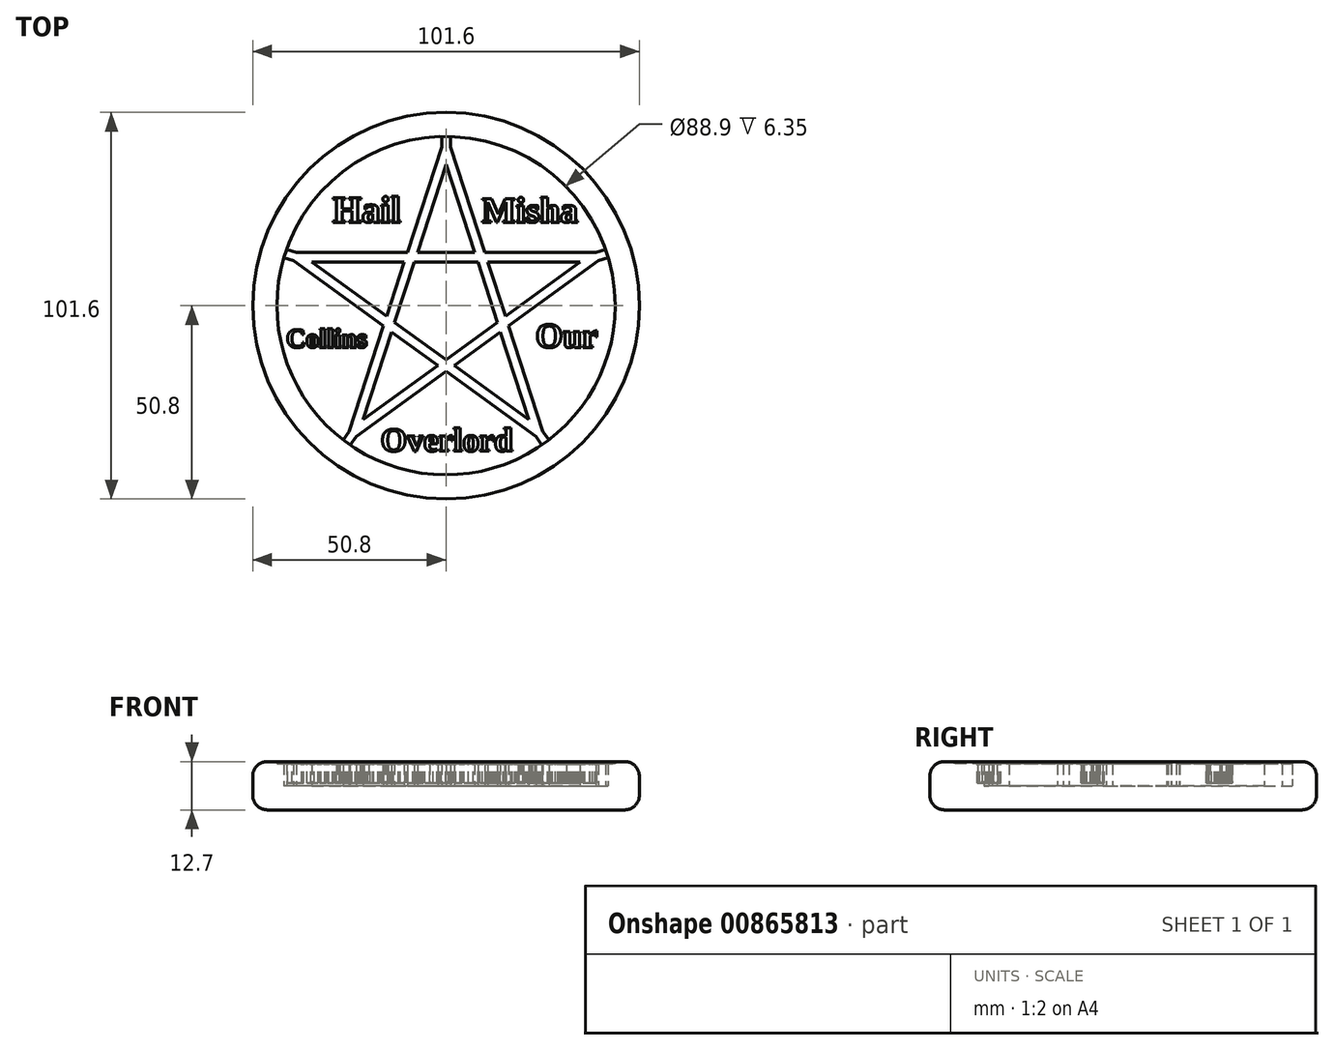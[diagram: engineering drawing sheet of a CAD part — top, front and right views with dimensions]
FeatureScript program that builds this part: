
annotation { "Feature Type Name" : "Feature", "Feature Type Description" : "" }
export const myFeature = defineFeature(function(context is Context, id is Id, definition is map)
    precondition{}
    {
        {
            var Q0;
            Q0=qCreatedBy(makeId("Top.planeOp"),FACE);
            var sketch = newSketch(context, id + "F0", { "sketchPlane" : qUnion([Q0])});
            skCircle(sketch, "E0", {"center": v(0, 0) * mm, "radius": 50.8 * mm});
            skSolve(sketch);
        }
        {
            var Q0;
            Q0=qSketchRegion(id+"F0",true);
            extrude(context, id + "F1", {"entities" : qUnion([Q0]), "depth" : 12.7 * mm, "offsetDistance" : 25.4 * mm});
        }
        {
            var Q0;
            Q0=makeQuery(id+"F1.opExtrude","CAP_FACE",FACE,{"disambiguationData":[OSD([sQuery(id+"F0.wireOp",EDGE,"E0")])],"isStart":false});
            shell(context, id + "F2", {"entities" : qUnion([Q0]), "thickness" : 6.35 * mm});
        }
        {
            var Q0;
            {var subQ0=sQuery(id+"F0.wireOp",EDGE,"E0");Q0=makeQuery(id+"F2.opShell","OFFSET_FACE",FACE,{"disambiguationData":[OSD([subQ0]),TDD([makeQuery(id+"F1.opExtrude","CAP_FACE",FACE,{"disambiguationData":[OSD([subQ0])],"isStart":true})])]});}
            var sketch = newSketch(context, id + "F3", { "sketchPlane" : qUnion([Q0])});
            skCircle(sketch, "E1.cCircle", {"center": v(0, 0) * mm, "radius": 13.97 * mm, "construction": true});
            skLineSegment(sketch, "E2", {"start": v(-10.15, 13.97) * mm, "end": v(-1.12, 41.75) * mm});
            skLineSegment(sketch, "E3", {"start": v(10.15, 13.97) * mm, "end": v(1.12, 41.75) * mm});
            skLineSegment(sketch, "E4", {"start": v(-16.42, -5.34) * mm, "end": v(-40.05, 11.83) * mm});
            skLineSegment(sketch, "E5", {"start": v(-10.15, 13.97) * mm, "end": v(-39.36, 13.97) * mm});
            skLineSegment(sketch, "E6", {"start": v(10.15, 13.97) * mm, "end": v(39.36, 13.97) * mm});
            skLineSegment(sketch, "E7", {"start": v(16.42, -5.34) * mm, "end": v(40.05, 11.83) * mm});
            skLineSegment(sketch, "E8", {"start": v(0, -17.27) * mm, "end": v(-23.63, -34.44) * mm});
            skLineSegment(sketch, "E9", {"start": v(-16.42, -5.34) * mm, "end": v(-25.45, -33.12) * mm});
            skLineSegment(sketch, "E10", {"start": v(16.42, -5.34) * mm, "end": v(25.45, -33.12) * mm});
            skLineSegment(sketch, "E11", {"start": v(0, -17.27) * mm, "end": v(23.63, -34.44) * mm});
            skLineSegment(sketch, "E12", {"start": v(39.36, 13.97) * mm, "end": v(41.93, 14.76) * mm});
            skLineSegment(sketch, "E13", {"start": v(40.05, 11.83) * mm, "end": v(42.62, 12.62) * mm});
            skLineSegment(sketch, "E14", {"start": v(1.12, 41.75) * mm, "end": v(1.12, 44.44) * mm});
            skLineSegment(sketch, "E15", {"start": v(-1.12, 41.75) * mm, "end": v(-1.12, 44.44) * mm});
            skLineSegment(sketch, "E16", {"start": v(-39.36, 13.97) * mm, "end": v(-41.91, 14.8) * mm});
            skLineSegment(sketch, "E17", {"start": v(-40.05, 11.83) * mm, "end": v(-42.6, 12.66) * mm});
            skLineSegment(sketch, "E18", {"start": v(-23.63, -34.44) * mm, "end": v(-25.2, -36.6) * mm});
            skLineSegment(sketch, "E19", {"start": v(-25.45, -33.12) * mm, "end": v(-27.03, -35.29) * mm});
            skLineSegment(sketch, "E20", {"start": v(-7.5, 13.97) * mm, "end": v(7.5, 13.97) * mm});
            skLineSegment(sketch, "E21", {"start": v(7.5, 13.97) * mm, "end": v(0, 37.06) * mm});
            skLineSegment(sketch, "E22", {"start": v(0, 37.06) * mm, "end": v(-7.5, 13.97) * mm});
            skLineSegment(sketch, "E23", {"start": v(-10.97, 11.45) * mm, "end": v(-35.25, 11.45) * mm});
            skLineSegment(sketch, "E24", {"start": v(-35.25, 11.45) * mm, "end": v(-15.6, -2.82) * mm});
            skPoint(sketch, "E25", {"position": v(-25.43, 4.32) * mm});
            skPoint(sketch, "E26", {"position": v(-28.24, 3.25) * mm});
            skPoint(sketch, "E27", {"position": v(-24.75, 13.97) * mm});
            skLineSegment(sketch, "E28", {"start": v(-14.28, -6.9) * mm, "end": v(-2.14, -15.71) * mm});
            skLineSegment(sketch, "E29", {"start": v(-2.14, -15.71) * mm, "end": v(-21.79, -29.99) * mm});
            skLineSegment(sketch, "E30", {"start": v(-21.79, -29.99) * mm, "end": v(-14.28, -6.9) * mm});
            skPoint(sketch, "E31", {"position": v(-11.96, -22.85) * mm});
            skPoint(sketch, "E32", {"position": v(-11.82, -25.85) * mm});
            skPoint(sketch, "E33", {"position": v(-18.03, -18.44) * mm});
            skPoint(sketch, "E34", {"position": v(-20.94, -19.23) * mm});
            skPoint(sketch, "E35.positionSnap0", {"position": v(-8.21, -11.3) * mm});
            skLineSegment(sketch, "E36", {"start": v(25.45, -33.12) * mm, "end": v(27.03, -35.29) * mm});
            skLineSegment(sketch, "E37", {"start": v(23.63, -34.44) * mm, "end": v(25.2, -36.6) * mm});
            skLineSegment(sketch, "E38", {"start": v(2.14, -15.71) * mm, "end": v(14.28, -6.9) * mm});
            skLineSegment(sketch, "E39", {"start": v(14.28, -6.9) * mm, "end": v(21.79, -29.99) * mm});
            skLineSegment(sketch, "E40", {"start": v(21.79, -29.99) * mm, "end": v(2.14, -15.71) * mm});
            skPoint(sketch, "E41", {"position": v(11.82, -25.85) * mm});
            skPoint(sketch, "E42.positionSnap0", {"position": v(20.94, -19.23) * mm});
            skLineSegment(sketch, "E43", {"start": v(10.97, 11.45) * mm, "end": v(15.6, -2.82) * mm});
            skLineSegment(sketch, "E44", {"start": v(15.6, -2.82) * mm, "end": v(35.25, 11.45) * mm});
            skLineSegment(sketch, "E45", {"start": v(35.25, 11.45) * mm, "end": v(10.97, 11.45) * mm});
            skPoint(sketch, "E46", {"position": v(23.1, 11.45) * mm});
            skPoint(sketch, "E47", {"position": v(24.75, 13.97) * mm});
            skPoint(sketch, "E48", {"position": v(13.29, 4.32) * mm});
            skCircle(sketch, "E49.cCircle", {"center": v(0, 0) * mm, "radius": 14.23 * mm, "construction": true});
            skLineSegment(sketch, "E49.0", {"start": v(13.53, -4.4) * mm, "end": v(0, -14.23) * mm});
            skLineSegment(sketch, "E49.1", {"start": v(0, -14.23) * mm, "end": v(-13.53, -4.4) * mm});
            skLineSegment(sketch, "E49.2", {"start": v(-13.53, -4.4) * mm, "end": v(-8.36, 11.51) * mm});
            skLineSegment(sketch, "E49.3", {"start": v(-8.36, 11.51) * mm, "end": v(8.36, 11.51) * mm});
            skLineSegment(sketch, "E49.4", {"start": v(8.36, 11.51) * mm, "end": v(13.53, -4.4) * mm});
            skLineSegment(sketch, "E50", {"start": v(-10.97, 11.45) * mm, "end": v(-15.6, -2.82) * mm});
            skPoint(sketch, "E51", {"position": v(-13.29, 4.32) * mm});
            skPoint(sketch, "E52", {"position": v(28.24, 3.25) * mm});
            skPoint(sketch, "E53.positionSnap0", {"position": v(25.43, 4.32) * mm});
            skPoint(sketch, "E54", {"position": v(-23.1, 11.45) * mm});
            skPoint(sketch, "E55", {"position": v(0, 13.97) * mm});
            skPoint(sketch, "E56", {"position": v(8.21, -11.3) * mm});
            skSolve(sketch);
        }
        {
            var Q0;
            Q0=makeQuery(id+"F1.opExtrude","CAP_EDGE",EDGE,{"disambiguationData":[OSD([sQuery(id+"F0.wireOp",EDGE,"E0")])],"isStart":false});
            fillet(context, id + "F4", {"entities" : qUnion([Q0]), "radius" : 3.8 * mm, "tangentPropagation" : true, "allowEdgeOverflow" : false});
        }
        {
            var Q0;
            Q0=makeQuery(id+"F1.opExtrude","CAP_EDGE",EDGE,{"disambiguationData":[OSD([sQuery(id+"F0.wireOp",EDGE,"E0")])],"isStart":true});
            fillet(context, id + "F5", {"entities" : qUnion([Q0]), "radius" : 3.8 * mm, "tangentPropagation" : true, "allowEdgeOverflow" : false});
        }
        {
            var Q0;
            Q0=makeQuery(id+"F3.imprint","IMPRINT",FACE,{"disambiguationData":[TD([[makeQuery(id+"F3.imprint","IMPRINT",EDGE,{"derivedFrom":sQuery(id+"F3.wireOp",EDGE,"E2")}),1.0]])]});
            var Q1;
            Q1=makeQuery(id+"F3.imprint","IMPRINT",FACE,{"disambiguationData":[TD([[makeQuery(id+"F3.imprint","IMPRINT",EDGE,{"derivedFrom":sQuery(id+"F3.wireOp",EDGE,"E20")}),1.0]])]});
            var Q2;
            Q2=makeQuery(id+"F3.imprint","IMPRINT",FACE,{"disambiguationData":[TD([[makeQuery(id+"F3.imprint","IMPRINT",EDGE,{"derivedFrom":sQuery(id+"F3.wireOp",EDGE,"E3")}),-1.0]])]});
            var Q3;
            Q3=makeQuery(id+"F3.imprint","IMPRINT",FACE,{"disambiguationData":[TD([[makeQuery(id+"F3.imprint","IMPRINT",EDGE,{"derivedFrom":sQuery(id+"F3.wireOp",EDGE,"E49.0")}),-1.0]])]});
            var Q4;
            Q4=makeQuery(id+"F3.imprint","IMPRINT",FACE,{"disambiguationData":[TD([[makeQuery(id+"F3.imprint","IMPRINT",EDGE,{"derivedFrom":sQuery(id+"F3.wireOp",EDGE,"E43")}),1.0]])]});
            var Q5;
            Q5=makeQuery(id+"F3.imprint","IMPRINT",FACE,{"disambiguationData":[TD([[makeQuery(id+"F3.imprint","IMPRINT",EDGE,{"derivedFrom":sQuery(id+"F3.wireOp",EDGE,"E7")}),-1.0]])]});
            var Q6;
            Q6=makeQuery(id+"F3.imprint","IMPRINT",FACE,{"disambiguationData":[TD([[makeQuery(id+"F3.imprint","IMPRINT",EDGE,{"derivedFrom":sQuery(id+"F3.wireOp",EDGE,"E38")}),-1.0]])]});
            var Q7;
            Q7=makeQuery(id+"F3.imprint","IMPRINT",FACE,{"disambiguationData":[TD([[makeQuery(id+"F3.imprint","IMPRINT",EDGE,{"derivedFrom":sQuery(id+"F3.wireOp",EDGE,"E8")}),1.0]])]});
            var Q8;
            Q8=makeQuery(id+"F3.imprint","IMPRINT",FACE,{"disambiguationData":[TD([[makeQuery(id+"F3.imprint","IMPRINT",EDGE,{"derivedFrom":sQuery(id+"F3.wireOp",EDGE,"E28")}),-1.0]])]});
            var Q9;
            Q9=makeQuery(id+"F3.imprint","IMPRINT",FACE,{"disambiguationData":[TD([[makeQuery(id+"F3.imprint","IMPRINT",EDGE,{"derivedFrom":sQuery(id+"F3.wireOp",EDGE,"E4")}),1.0]])]});
            var Q10;
            Q10=makeQuery(id+"F3.imprint","IMPRINT",FACE,{"disambiguationData":[TD([[makeQuery(id+"F3.imprint","IMPRINT",EDGE,{"derivedFrom":sQuery(id+"F3.wireOp",EDGE,"E23")}),1.0]])]});
            extrude(context, id + "F6", {"entities" : qUnion([Q0, Q1, Q2, Q3, Q4, Q5, Q6, Q7, Q8, Q9, Q10]), "operationType" : NewBodyOperationType.ADD, "depth" : 5.84 * mm, "offsetDistance" : 25.4 * mm});
        }
        {
            var Q0;
            Q0=makeQuery(id+"F6.opExtrude","CAP_FACE",FACE,{"disambiguationData":[OSD([sQuery(id+"F0.wireOp",EDGE,"E0"),sQuery(id+"F3.wireOp",EDGE,"E2"),sQuery(id+"F3.wireOp",EDGE,"E5"),sQuery(id+"F3.wireOp",EDGE,"E15"),sQuery(id+"F3.wireOp",EDGE,"E16")])],"isStart":false});
            var sketch = newSketch(context, id + "F7", { "sketchPlane" : qUnion([Q0])});
            skText(sketch, "E57", { "text": "Hail", "fontName": "Tinos-Bold.ttf"});
            skText(sketch, "E58", { "text": "Misha", "fontName": "Tinos-Bold.ttf"});
            skText(sketch, "E59", { "text": "Overlord", "fontName": "Tinos-Bold.ttf"});
            skText(sketch, "E60", { "text": "Collins", "fontName": "Tinos-Bold.ttf"});
            skText(sketch, "E61", { "text": "Our", "fontName": "Tinos-Bold.ttf"});
            const initialGuessF7  = {"E57": [-0.0298, 0.02192, 1, 0, 0.00706], "E58": [0.00941, 0.02192, 1, 0, 0.00682], "E59": [-0.01714, -0.03824, 1, 0, 0.00633], "E60": [-0.042, -0.01096, 1, 0, 0.00511], "E61": [0.02355, -0.01096, 1, 0, 0.00658]};
            skSetInitialGuess(sketch, initialGuessF7);
            skSolve(sketch);
        }
        {
            var Q0;
            Q0 = qSketchRegion(id + "F7", true);
            extrude(context, id + "F8", {"entities" : qUnion([Q0]), "operationType" : NewBodyOperationType.REMOVE, "oppositeDirection" : true, "depth" : 5.08 * mm, "offsetDistance" : 25.4 * mm});
        }
    });
